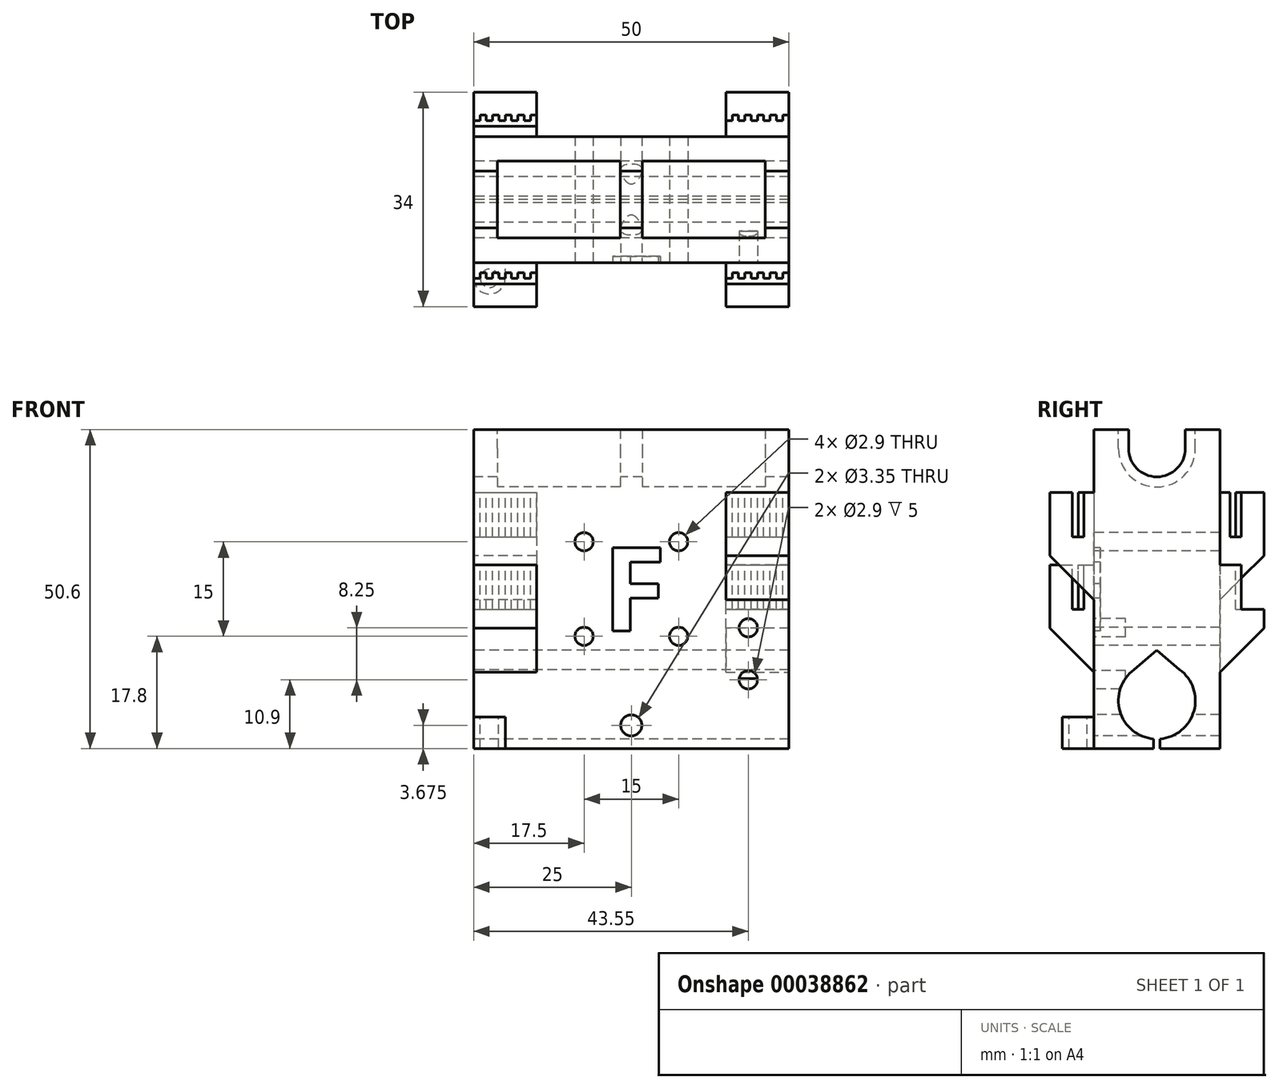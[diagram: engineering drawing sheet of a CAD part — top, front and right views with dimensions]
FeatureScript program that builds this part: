
annotation { "Feature Type Name" : "Feature", "Feature Type Description" : "" }
export const myFeature = defineFeature(function(context is Context, id is Id, definition is map)
    precondition{}
    {
        {
            assignVariable(context, id + "F0", {"name" : "LM8LUU", "anyValue" : 0});
        }
        {
            var Q0;
            Q0=qCreatedBy(makeId("Top.planeOp"),FACE);
            var sketch = newSketch(context, id + "F1", { "sketchPlane" : qUnion([Q0])});
            skLineSegment(sketch, "E0.bottom", {"start": v(0, 0) * mm, "end": v(50, 0) * mm});
            skLineSegment(sketch, "E0.top", {"start": v(0, 20) * mm, "end": v(50, 20) * mm});
            skLineSegment(sketch, "E0.left", {"start": v(0, 0) * mm, "end": v(0, 20) * mm});
            skLineSegment(sketch, "E0.right", {"start": v(50, 0) * mm, "end": v(50, 20) * mm});
            skSolve(sketch);
        }
        {
            var Q0;
            Q0=qSketchRegion(id+"F1",true);
            extrude(context, id + "F2", {"entities" : qUnion([Q0]), "depth" : 50.6 * mm});
        }
        {
            var Q0;
            Q0=makeQuery(id+"F2.opExtrude","SWEPT_FACE",FACE,{"disambiguationData":[OSD([sQuery(id+"F1.wireOp",EDGE,"E0.left")])]});
            var sketch = newSketch(context, id + "F3", { "sketchPlane" : qUnion([Q0])});
            skCircle(sketch, "E1", {"center": v(-10, 7.6) * mm, "radius": 6.1 * mm});
            skCircle(sketch, "E2", {"center": v(-10, 47.6) * mm, "radius": 4.5 * mm});
            skLineSegment(sketch, "E3", {"start": v(-20, 47.6) * mm, "end": v(0, 47.6) * mm, "construction": true});
            skLineSegment(sketch, "E4", {"start": v(-14.5, 50.6) * mm, "end": v(-14.5, 47.6) * mm});
            skLineSegment(sketch, "E5", {"start": v(-5.5, 50.6) * mm, "end": v(-5.5, 47.6) * mm});
            skLineSegment(sketch, "E6", {"start": v(-20, 7.6) * mm, "end": v(0, 7.6) * mm, "construction": true});
            skLineSegment(sketch, "E7", {"start": v(-10, 7.6) * mm, "end": v(-10, 0) * mm, "construction": true});
            skLineSegment(sketch, "E8", {"start": v(-10, 0) * mm, "end": v(-10.5, 0) * mm});
            skLineSegment(sketch, "E9", {"start": v(-10.5, 0) * mm, "end": v(-10.5, 1.52) * mm});
            skLineSegment(sketch, "E10", {"start": v(-10.5, 1.52) * mm, "end": v(-9.5, 1.52) * mm});
            skLineSegment(sketch, "E11", {"start": v(-9.5, 1.52) * mm, "end": v(-9.5, 0) * mm});
            skLineSegment(sketch, "E12", {"start": v(-9.5, 0) * mm, "end": v(-10, 0) * mm});
            skLineSegment(sketch, "E13", {"start": v(-10, 13.7) * mm, "end": v(-10, 15.6) * mm});
            skLineSegment(sketch, "E14", {"start": v(-10, 15.6) * mm, "end": v(-6.39, 12.51) * mm});
            skLineSegment(sketch, "E15", {"start": v(-10, 15.6) * mm, "end": v(-13.61, 12.51) * mm});
            skCircle(sketch, "E16", {"center": v(-10, 47.6) * mm, "radius": 6.1 * mm});
            skLineSegment(sketch, "E17", {"start": v(-3.9, 47.6) * mm, "end": v(-3.9, 50.6) * mm});
            skLineSegment(sketch, "E18", {"start": v(-16.1, 47.6) * mm, "end": v(-16.1, 50.6) * mm});
            skSolve(sketch);
        }
        {
            var Q0;
            {var subQ0=sQuery(id+"F3.wireOp",EDGE,"E14");var subQ1=sQuery(id+"F3.wireOp",EDGE,"E1");var subQ3=makeQuery(id+"F3.imprint","INTERSECT",VERTEX,{"disambiguationData":[OD(0.0)],"derivedFrom":[subQ1,subQ0]});Q0=makeQuery(id+"F3.imprint","IMPRINT",FACE,{"disambiguationData":[TD([[makeQuery(id+"F3.imprint","IMPRINT",EDGE,{"disambiguationData":[TD([[subQ3,-1.0]])],"derivedFrom":subQ1}),1.0]])]});}
            var Q1;
            {var subQ0=sQuery(id+"F3.wireOp",EDGE,"E15");var subQ1=sQuery(id+"F3.wireOp",EDGE,"E1");var subQ3=makeQuery(id+"F3.imprint","INTERSECT",VERTEX,{"disambiguationData":[OD(0.0)],"derivedFrom":[subQ1,subQ0]});Q1=makeQuery(id+"F3.imprint","IMPRINT",FACE,{"disambiguationData":[TD([[makeQuery(id+"F3.imprint","IMPRINT",EDGE,{"disambiguationData":[TD([[subQ3,1.0]])],"derivedFrom":subQ1}),1.0]])]});}
            var Q2;
            Q2=makeQuery(id+"F3.imprint","IMPRINT",FACE,{"disambiguationData":[TD([[makeQuery(id+"F3.imprint","IMPRINT",EDGE,{"derivedFrom":sQuery(id+"F3.wireOp",EDGE,"E8")}),-1.0]])]});
            var Q3;
            {var subQ0=sQuery(id+"F3.wireOp",EDGE,"E10");Q3=makeQuery(id+"F3.imprint","IMPRINT",FACE,{"disambiguationData":[TD([[makeQuery(id+"F3.imprint","IMPRINT",EDGE,{"derivedFrom":subQ0}),-1.0]])]});}
            var Q4;
            {var subQ3=sQuery(id+"F3.wireOp",EDGE,"E13");Q4=makeQuery(id+"F3.imprint","IMPRINT",FACE,{"disambiguationData":[TD([[makeQuery(id+"F3.imprint","IMPRINT",EDGE,{"derivedFrom":subQ3}),-1.0]])]});}
            var Q5;
            {var subQ3=sQuery(id+"F3.wireOp",EDGE,"E13");Q5=makeQuery(id+"F3.imprint","IMPRINT",FACE,{"disambiguationData":[TD([[makeQuery(id+"F3.imprint","IMPRINT",EDGE,{"derivedFrom":subQ3}),1.0]])]});}
            var Q6;
            {var subQ7=sQuery(id+"F3.wireOp",EDGE,"E10");Q6=makeQuery(id+"F3.imprint","IMPRINT",FACE,{"disambiguationData":[TD([[makeQuery(id+"F3.imprint","IMPRINT",EDGE,{"derivedFrom":subQ7}),1.0]])]});}
            var Q7;
            {var subQ3=sQuery(id+"F3.wireOp",EDGE,"E5");Q7=makeQuery(id+"F3.imprint","IMPRINT",FACE,{"disambiguationData":[TD([[makeQuery(id+"F3.imprint","IMPRINT",EDGE,{"derivedFrom":subQ3}),-1.0]])]});}
            var Q8;
            {var subQ0=sQuery(id+"F3.wireOp",EDGE,"E4");Q8=makeQuery(id+"F3.imprint","IMPRINT",FACE,{"disambiguationData":[TD([[makeQuery(id+"F3.imprint","IMPRINT",EDGE,{"derivedFrom":subQ0}),1.0]])]});}
            var Q9;
            {var subQ0=sQuery(id+"F3.wireOp",EDGE,"E4");Q9=makeQuery(id+"F3.imprint","IMPRINT",FACE,{"disambiguationData":[TD([[makeQuery(id+"F3.imprint","IMPRINT",EDGE,{"derivedFrom":subQ0}),1.0]])]});}
            var Q10;
            {var subQ3=sQuery(id+"F3.wireOp",EDGE,"E5");Q10=makeQuery(id+"F3.imprint","IMPRINT",FACE,{"disambiguationData":[TD([[makeQuery(id+"F3.imprint","IMPRINT",EDGE,{"derivedFrom":subQ3}),-1.0]])]});}
            var Q11;
            {var subQ1=sQuery(id+"F3.wireOp",EDGE,"E2");var subQ4=makeQuery(id+"F3.imprint","INTERSECT",VERTEX,{"derivedFrom":[subQ1,sQuery(id+"F3.wireOp",EDGE,"E5")]});Q11=makeQuery(id+"F3.imprint","IMPRINT",FACE,{"disambiguationData":[TD([[makeQuery(id+"F3.imprint","IMPRINT",EDGE,{"disambiguationData":[TD([[subQ4,-1.0]])],"derivedFrom":subQ1}),1.0]])]});}
            extrude(context, id + "F4", {"entities" : qUnion([Q0, Q1, Q2, Q3, Q4, Q5, Q6, Q7, Q8, Q9, Q10, Q11]), "operationType" : NewBodyOperationType.REMOVE, "endBound" : BoundingType.THROUGH_ALL, "oppositeDirection" : true, "depth" : 25 * mm});
        }
        {
            var Q0;
            {var subQ3=sQuery(id+"F3.wireOp",EDGE,"E4");Q0=makeQuery(id+"F3.imprint","IMPRINT",FACE,{"disambiguationData":[TD([[makeQuery(id+"F3.imprint","IMPRINT",EDGE,{"derivedFrom":subQ3}),-1.0]])]});}
            var Q1;
            {var subQ3=sQuery(id+"F3.wireOp",EDGE,"E18");Q1=makeQuery(id+"F3.imprint","IMPRINT",FACE,{"disambiguationData":[TD([[makeQuery(id+"F3.imprint","IMPRINT",EDGE,{"derivedFrom":subQ3}),-1.0]])]});}
            var Q2;
            {var subQ3=sQuery(id+"F3.wireOp",EDGE,"E17");Q2=makeQuery(id+"F3.imprint","IMPRINT",FACE,{"disambiguationData":[TD([[makeQuery(id+"F3.imprint","IMPRINT",EDGE,{"derivedFrom":subQ3}),1.0]])]});}
            extrude(context, id + "F5", {"entities" : qUnion([Q0, Q1, Q2]), "operationType" : NewBodyOperationType.REMOVE, "oppositeDirection" : true, "depth" : (46.25 + getVariable(context, 'LM8LUU') * 2) * mm});
        }
        {
            var Q0;
            {var subQ3=sQuery(id+"F3.wireOp",EDGE,"E4");Q0=makeQuery(id+"F3.imprint","IMPRINT",FACE,{"disambiguationData":[TD([[makeQuery(id+"F3.imprint","IMPRINT",EDGE,{"derivedFrom":subQ3}),-1.0]])]});}
            var Q1;
            {var subQ3=sQuery(id+"F3.wireOp",EDGE,"E18");Q1=makeQuery(id+"F3.imprint","IMPRINT",FACE,{"disambiguationData":[TD([[makeQuery(id+"F3.imprint","IMPRINT",EDGE,{"derivedFrom":subQ3}),-1.0]])]});}
            var Q2;
            {var subQ3=sQuery(id+"F3.wireOp",EDGE,"E17");Q2=makeQuery(id+"F3.imprint","IMPRINT",FACE,{"disambiguationData":[TD([[makeQuery(id+"F3.imprint","IMPRINT",EDGE,{"derivedFrom":subQ3}),1.0]])]});}
            extrude(context, id + "F6", {"entities" : qUnion([Q0, Q1, Q2]), "operationType" : NewBodyOperationType.ADD, "oppositeDirection" : true, "depth" : (26.75 - getVariable(context, 'LM8LUU')) * mm});
        }
        {
            var Q0;
            {var subQ3=sQuery(id+"F3.wireOp",EDGE,"E4");Q0=makeQuery(id+"F3.imprint","IMPRINT",FACE,{"disambiguationData":[TD([[makeQuery(id+"F3.imprint","IMPRINT",EDGE,{"derivedFrom":subQ3}),-1.0]])]});}
            var Q1;
            {var subQ3=sQuery(id+"F3.wireOp",EDGE,"E18");Q1=makeQuery(id+"F3.imprint","IMPRINT",FACE,{"disambiguationData":[TD([[makeQuery(id+"F3.imprint","IMPRINT",EDGE,{"derivedFrom":subQ3}),-1.0]])]});}
            var Q2;
            {var subQ3=sQuery(id+"F3.wireOp",EDGE,"E17");Q2=makeQuery(id+"F3.imprint","IMPRINT",FACE,{"disambiguationData":[TD([[makeQuery(id+"F3.imprint","IMPRINT",EDGE,{"derivedFrom":subQ3}),1.0]])]});}
            extrude(context, id + "F7", {"entities" : qUnion([Q0, Q1, Q2]), "operationType" : NewBodyOperationType.REMOVE, "oppositeDirection" : true, "depth" : (23.25 + getVariable(context, 'LM8LUU')) * mm});
        }
        {
            var Q0;
            {var subQ3=sQuery(id+"F3.wireOp",EDGE,"E4");Q0=makeQuery(id+"F3.imprint","IMPRINT",FACE,{"disambiguationData":[TD([[makeQuery(id+"F3.imprint","IMPRINT",EDGE,{"derivedFrom":subQ3}),-1.0]])]});}
            var Q1;
            {var subQ3=sQuery(id+"F3.wireOp",EDGE,"E18");Q1=makeQuery(id+"F3.imprint","IMPRINT",FACE,{"disambiguationData":[TD([[makeQuery(id+"F3.imprint","IMPRINT",EDGE,{"derivedFrom":subQ3}),-1.0]])]});}
            var Q2;
            {var subQ3=sQuery(id+"F3.wireOp",EDGE,"E17");Q2=makeQuery(id+"F3.imprint","IMPRINT",FACE,{"disambiguationData":[TD([[makeQuery(id+"F3.imprint","IMPRINT",EDGE,{"derivedFrom":subQ3}),1.0]])]});}
            extrude(context, id + "F8", {"entities" : qUnion([Q0, Q1, Q2]), "operationType" : NewBodyOperationType.ADD, "oppositeDirection" : true, "depth" : 3.75 * mm});
        }
        {
            var Q0;
            Q0=makeQuery(id+"F2.opExtrude","SWEPT_FACE",FACE,{"disambiguationData":[OSD([sQuery(id+"F1.wireOp",EDGE,"E0.bottom")])]});
            var sketch = newSketch(context, id + "F9", { "sketchPlane" : qUnion([Q0])});
            skLineSegment(sketch, "E19.bottom", {"start": v(0, 29.1) * mm, "end": v(10, 29.1) * mm});
            skLineSegment(sketch, "E19.top", {"start": v(0, 9.1) * mm, "end": v(10, 9.1) * mm});
            skLineSegment(sketch, "E19.left", {"start": v(0, 29.1) * mm, "end": v(0, 9.1) * mm});
            skLineSegment(sketch, "E19.right", {"start": v(10, 29.1) * mm, "end": v(10, 9.1) * mm});
            skLineSegment(sketch, "E20.bottom", {"start": v(50, 40.6) * mm, "end": v(40, 40.6) * mm});
            skLineSegment(sketch, "E20.top", {"start": v(50, 20.6) * mm, "end": v(40, 20.6) * mm});
            skLineSegment(sketch, "E20.left", {"start": v(50, 40.6) * mm, "end": v(50, 20.6) * mm});
            skLineSegment(sketch, "E20.right", {"start": v(40, 40.6) * mm, "end": v(40, 20.6) * mm});
            skPoint(sketch, "E21", {"position": v(0, 47.6) * mm});
            skPoint(sketch, "E22", {"position": v(0, 8.6) * mm});
            skSolve(sketch);
        }
        {
            var Q0;
            Q0=qSketchRegion(id+"F9",true);
            extrude(context, id + "F10", {"entities" : qUnion([Q0]), "operationType" : NewBodyOperationType.ADD, "depth" : 7 * mm});
        }
        {
            var Q0;
            Q0=makeQuery(id+"F10.opExtrude","CAP_EDGE",EDGE,{"disambiguationData":[OSD([sQuery(id+"F9.wireOp",EDGE,"E19.top")])],"isStart":false});
            var Q1;
            Q1=makeQuery(id+"F10.opExtrude","CAP_EDGE",EDGE,{"disambiguationData":[OSD([sQuery(id+"F9.wireOp",EDGE,"E20.top")])],"isStart":false});
            chamfer(context, id + "F11", {"entities" : qUnion([Q0, Q1]), "width" : 10 * mm, "tangentPropagation" : true});
        }
        {
            var Q0;
            Q0=makeQuery(id+"F10.opExtrude","SWEPT_FACE",FACE,{"disambiguationData":[OSD([sQuery(id+"F9.wireOp",EDGE,"E19.bottom")])]});
            var sketch = newSketch(context, id + "F12", { "sketchPlane" : qUnion([Q0])});
            skLineSegment(sketch, "E23", {"start": v(-935.9, 0) * mm, "end": v(-935.88, -4.54) * mm});
            skLineSegment(sketch, "E24.left", {"start": v(0, -3.4) * mm, "end": v(0, -1.6) * mm});
            skLineSegment(sketch, "E25", {"start": v(6, -2.5) * mm, "end": v(7, -2.5) * mm});
            skLineSegment(sketch, "E26", {"start": v(4, -2.5) * mm, "end": v(5, -2.5) * mm});
            skLineSegment(sketch, "E27", {"start": v(0, -2.5) * mm, "end": v(1, -2.5) * mm});
            skLineSegment(sketch, "E28", {"start": v(7, -1.6) * mm, "end": v(8, -1.6) * mm});
            skLineSegment(sketch, "E29", {"start": v(2, -2.5) * mm, "end": v(3, -2.5) * mm});
            skLineSegment(sketch, "E30", {"start": v(3, -1.6) * mm, "end": v(4, -1.6) * mm});
            skLineSegment(sketch, "E31", {"start": v(8, -2.5) * mm, "end": v(9, -2.5) * mm});
            skLineSegment(sketch, "E32", {"start": v(8, -1.6) * mm, "end": v(8, -2.5) * mm});
            skLineSegment(sketch, "E33", {"start": v(9, -2.5) * mm, "end": v(9, -1.6) * mm});
            skLineSegment(sketch, "E34", {"start": v(10, -1.6) * mm, "end": v(10, -2.5) * mm});
            skLineSegment(sketch, "E35", {"start": v(6, -1.6) * mm, "end": v(6, -2.5) * mm});
            skLineSegment(sketch, "E36", {"start": v(2, -1.6) * mm, "end": v(2, -2.5) * mm});
            skLineSegment(sketch, "E37", {"start": v(1, -1.6) * mm, "end": v(2, -1.6) * mm});
            skLineSegment(sketch, "E38", {"start": v(1, -2.5) * mm, "end": v(1, -1.6) * mm});
            skLineSegment(sketch, "E39", {"start": v(9, -1.6) * mm, "end": v(10, -1.6) * mm});
            skLineSegment(sketch, "E40", {"start": v(5, -1.6) * mm, "end": v(6, -1.6) * mm});
            skLineSegment(sketch, "E41", {"start": v(5, -2.5) * mm, "end": v(5, -1.6) * mm});
            skLineSegment(sketch, "E42", {"start": v(3, -2.5) * mm, "end": v(3, -1.6) * mm});
            skLineSegment(sketch, "E43", {"start": v(4, -1.6) * mm, "end": v(4, -2.5) * mm});
            skLineSegment(sketch, "E44", {"start": v(7, -2.5) * mm, "end": v(7, -1.6) * mm});
            skLineSegment(sketch, "E45", {"start": v(0, -1.6) * mm, "end": v(0, -2.5) * mm});
            skLineSegment(sketch, "E46", {"start": v(10, -2.5) * mm, "end": v(10, -3.4) * mm});
            skLineSegment(sketch, "E47", {"start": v(0, -3.4) * mm, "end": v(10, -3.4) * mm});
            skLineSegment(sketch, "E48", {"start": v(5.3, -1.6) * mm, "end": v(5.3, 0) * mm});
            skSolve(sketch);
        }
        {
            var Q0;
            Q0=qSketchRegion(id+"F12",true);
            extrude(context, id + "F13", {"entities" : qUnion([Q0]), "operationType" : NewBodyOperationType.REMOVE, "oppositeDirection" : true, "depth" : 7 * mm});
        }
        {
            var Q0;
            Q0=makeQuery(id+"F10.opExtrude","SWEPT_FACE",FACE,{"disambiguationData":[OSD([sQuery(id+"F9.wireOp",EDGE,"E20.bottom")])]});
            var sketch = newSketch(context, id + "F14", { "sketchPlane" : qUnion([Q0])});
            skLineSegment(sketch, "E49.left", {"start": v(40, -3.4) * mm, "end": v(40, -1.6) * mm});
            skLineSegment(sketch, "E50", {"start": v(46, -2.5) * mm, "end": v(47, -2.5) * mm});
            skLineSegment(sketch, "E51", {"start": v(44, -2.5) * mm, "end": v(45, -2.5) * mm});
            skLineSegment(sketch, "E52", {"start": v(40, -2.5) * mm, "end": v(41, -2.5) * mm});
            skLineSegment(sketch, "E53", {"start": v(47, -1.6) * mm, "end": v(48, -1.6) * mm});
            skLineSegment(sketch, "E54", {"start": v(42, -2.5) * mm, "end": v(43, -2.5) * mm});
            skLineSegment(sketch, "E55", {"start": v(43, -1.6) * mm, "end": v(44, -1.6) * mm});
            skLineSegment(sketch, "E56", {"start": v(48, -2.5) * mm, "end": v(49, -2.5) * mm});
            skLineSegment(sketch, "E57", {"start": v(48, -1.6) * mm, "end": v(48, -2.5) * mm});
            skLineSegment(sketch, "E58", {"start": v(49, -2.5) * mm, "end": v(49, -1.6) * mm});
            skLineSegment(sketch, "E59", {"start": v(50, -1.6) * mm, "end": v(50, -2.5) * mm});
            skLineSegment(sketch, "E60", {"start": v(46, -1.6) * mm, "end": v(46, -2.5) * mm});
            skLineSegment(sketch, "E61", {"start": v(42, -1.6) * mm, "end": v(42, -2.5) * mm});
            skLineSegment(sketch, "E62", {"start": v(41, -1.6) * mm, "end": v(42, -1.6) * mm});
            skLineSegment(sketch, "E63", {"start": v(41, -2.5) * mm, "end": v(41, -1.6) * mm});
            skLineSegment(sketch, "E64", {"start": v(49, -1.6) * mm, "end": v(50, -1.6) * mm});
            skLineSegment(sketch, "E65", {"start": v(45, -1.6) * mm, "end": v(46, -1.6) * mm});
            skLineSegment(sketch, "E66", {"start": v(45, -2.5) * mm, "end": v(45, -1.6) * mm});
            skLineSegment(sketch, "E67", {"start": v(43, -2.5) * mm, "end": v(43, -1.6) * mm});
            skLineSegment(sketch, "E68", {"start": v(44, -1.6) * mm, "end": v(44, -2.5) * mm});
            skLineSegment(sketch, "E69", {"start": v(47, -2.5) * mm, "end": v(47, -1.6) * mm});
            skLineSegment(sketch, "E70", {"start": v(40, -1.6) * mm, "end": v(40, -2.5) * mm});
            skLineSegment(sketch, "E71", {"start": v(50, -2.5) * mm, "end": v(50, -3.4) * mm});
            skLineSegment(sketch, "E72", {"start": v(40, -3.4) * mm, "end": v(50, -3.4) * mm});
            skLineSegment(sketch, "E73", {"start": v(45.23, -1.6) * mm, "end": v(45.23, 0) * mm});
            skSolve(sketch);
        }
        {
            var Q0;
            Q0=qSketchRegion(id+"F14",true);
            extrude(context, id + "F15", {"entities" : qUnion([Q0]), "operationType" : NewBodyOperationType.REMOVE, "oppositeDirection" : true, "depth" : 7 * mm});
        }
        {
            var Q0;
            Q0=makeQuery(id+"F2.opExtrude","SWEPT_FACE",FACE,{"disambiguationData":[OSD([sQuery(id+"F1.wireOp",EDGE,"E0.top")])]});
            var sketch = newSketch(context, id + "F16", { "sketchPlane" : qUnion([Q0])});
            skLineSegment(sketch, "E74.bottom", {"start": v(-50, 9.1) * mm, "end": v(-40, 9.1) * mm});
            skLineSegment(sketch, "E74.top", {"start": v(-50, 29.1) * mm, "end": v(-40, 29.1) * mm});
            skLineSegment(sketch, "E74.left", {"start": v(-50, 9.1) * mm, "end": v(-50, 29.1) * mm});
            skLineSegment(sketch, "E74.right", {"start": v(-40, 9.1) * mm, "end": v(-40, 29.1) * mm});
            skLineSegment(sketch, "E75.bottom", {"start": v(0, 40.6) * mm, "end": v(-10, 40.6) * mm});
            skLineSegment(sketch, "E75.top", {"start": v(0, 20.6) * mm, "end": v(-10, 20.6) * mm});
            skLineSegment(sketch, "E75.left", {"start": v(0, 40.6) * mm, "end": v(0, 20.6) * mm});
            skLineSegment(sketch, "E75.right", {"start": v(-10, 40.6) * mm, "end": v(-10, 20.6) * mm});
            skSolve(sketch);
        }
        {
            var Q0;
            Q0=qSketchRegion(id+"F16",true);
            extrude(context, id + "F17", {"entities" : qUnion([Q0]), "operationType" : NewBodyOperationType.ADD, "depth" : 7 * mm});
        }
        {
            var Q0;
            Q0=makeQuery(id+"F17.opExtrude","SWEPT_FACE",FACE,{"disambiguationData":[OSD([sQuery(id+"F16.wireOp",EDGE,"E74.top")])]});
            var sketch = newSketch(context, id + "F18", { "sketchPlane" : qUnion([Q0])});
            skLineSegment(sketch, "E76.left", {"start": v(40, 21.6) * mm, "end": v(40, 23.4) * mm});
            skLineSegment(sketch, "E77", {"start": v(46, 22.5) * mm, "end": v(47, 22.5) * mm});
            skLineSegment(sketch, "E78", {"start": v(44, 22.5) * mm, "end": v(45, 22.5) * mm});
            skLineSegment(sketch, "E79", {"start": v(40, 22.5) * mm, "end": v(41, 22.5) * mm});
            skLineSegment(sketch, "E80", {"start": v(47, 23.4) * mm, "end": v(48, 23.4) * mm});
            skLineSegment(sketch, "E81", {"start": v(42, 22.5) * mm, "end": v(43, 22.5) * mm});
            skLineSegment(sketch, "E82", {"start": v(43, 23.4) * mm, "end": v(44, 23.4) * mm});
            skLineSegment(sketch, "E83", {"start": v(48, 22.5) * mm, "end": v(49, 22.5) * mm});
            skLineSegment(sketch, "E84", {"start": v(48, 23.4) * mm, "end": v(48, 22.5) * mm});
            skLineSegment(sketch, "E85", {"start": v(49, 22.5) * mm, "end": v(49, 23.4) * mm});
            skLineSegment(sketch, "E86", {"start": v(50, 23.4) * mm, "end": v(50, 22.5) * mm});
            skLineSegment(sketch, "E87", {"start": v(46, 23.4) * mm, "end": v(46, 22.5) * mm});
            skLineSegment(sketch, "E88", {"start": v(42, 23.4) * mm, "end": v(42, 22.5) * mm});
            skLineSegment(sketch, "E89", {"start": v(41, 23.4) * mm, "end": v(42, 23.4) * mm});
            skLineSegment(sketch, "E90", {"start": v(41, 22.5) * mm, "end": v(41, 23.4) * mm});
            skLineSegment(sketch, "E91", {"start": v(49, 23.4) * mm, "end": v(50, 23.4) * mm});
            skLineSegment(sketch, "E92", {"start": v(45, 23.4) * mm, "end": v(46, 23.4) * mm});
            skLineSegment(sketch, "E93", {"start": v(45, 22.5) * mm, "end": v(45, 23.4) * mm});
            skLineSegment(sketch, "E94", {"start": v(43, 22.5) * mm, "end": v(43, 23.4) * mm});
            skLineSegment(sketch, "E95", {"start": v(44, 23.4) * mm, "end": v(44, 22.5) * mm});
            skLineSegment(sketch, "E96", {"start": v(47, 22.5) * mm, "end": v(47, 23.4) * mm});
            skLineSegment(sketch, "E97", {"start": v(40, 23.4) * mm, "end": v(40, 22.5) * mm});
            skLineSegment(sketch, "E98", {"start": v(50, 22.5) * mm, "end": v(50, 21.6) * mm});
            skLineSegment(sketch, "E99", {"start": v(40, 21.6) * mm, "end": v(50, 21.6) * mm});
            skLineSegment(sketch, "E100", {"start": v(45, 21.6) * mm, "end": v(45, 20) * mm});
            skSolve(sketch);
        }
        {
            var Q0;
            {var subQ4=sQuery(id+"F18.wireOp",EDGE,"E76.left");Q0=makeQuery(id+"F18.imprint","IMPRINT",FACE,{"disambiguationData":[TD([[makeQuery(id+"F18.imprint","IMPRINT",EDGE,{"derivedFrom":subQ4}),1.0]])]});}
            extrude(context, id + "F19", {"entities" : qUnion([Q0]), "operationType" : NewBodyOperationType.REMOVE, "oppositeDirection" : true, "depth" : 7 * mm});
        }
        {
            var Q0;
            Q0=makeQuery(id+"F17.opExtrude","SWEPT_FACE",FACE,{"disambiguationData":[OSD([sQuery(id+"F16.wireOp",EDGE,"E75.bottom")])]});
            var sketch = newSketch(context, id + "F20", { "sketchPlane" : qUnion([Q0])});
            skLineSegment(sketch, "E101", {"start": v(6, 22.5) * mm, "end": v(7, 22.5) * mm});
            skLineSegment(sketch, "E102", {"start": v(4, 22.5) * mm, "end": v(5, 22.5) * mm});
            skLineSegment(sketch, "E103", {"start": v(0, 22.5) * mm, "end": v(1, 22.5) * mm});
            skLineSegment(sketch, "E104", {"start": v(7, 23.4) * mm, "end": v(8, 23.4) * mm});
            skLineSegment(sketch, "E105", {"start": v(2, 22.5) * mm, "end": v(3, 22.5) * mm});
            skLineSegment(sketch, "E106", {"start": v(3, 23.4) * mm, "end": v(4, 23.4) * mm});
            skLineSegment(sketch, "E107", {"start": v(8, 22.5) * mm, "end": v(9, 22.5) * mm});
            skLineSegment(sketch, "E108", {"start": v(8, 23.4) * mm, "end": v(8, 22.5) * mm});
            skLineSegment(sketch, "E109", {"start": v(9, 22.5) * mm, "end": v(9, 23.4) * mm});
            skLineSegment(sketch, "E110", {"start": v(10, 23.4) * mm, "end": v(10, 22.5) * mm});
            skLineSegment(sketch, "E111", {"start": v(6, 23.4) * mm, "end": v(6, 22.5) * mm});
            skLineSegment(sketch, "E112", {"start": v(2, 23.4) * mm, "end": v(2, 22.5) * mm});
            skLineSegment(sketch, "E113", {"start": v(1, 23.4) * mm, "end": v(2, 23.4) * mm});
            skLineSegment(sketch, "E114", {"start": v(1, 22.5) * mm, "end": v(1, 23.4) * mm});
            skLineSegment(sketch, "E115", {"start": v(9, 23.4) * mm, "end": v(10, 23.4) * mm});
            skLineSegment(sketch, "E116", {"start": v(5, 23.4) * mm, "end": v(6, 23.4) * mm});
            skLineSegment(sketch, "E117", {"start": v(5, 22.5) * mm, "end": v(5, 23.4) * mm});
            skLineSegment(sketch, "E118", {"start": v(3, 22.5) * mm, "end": v(3, 23.4) * mm});
            skLineSegment(sketch, "E119", {"start": v(4, 23.4) * mm, "end": v(4, 22.5) * mm});
            skLineSegment(sketch, "E120", {"start": v(7, 22.5) * mm, "end": v(7, 23.4) * mm});
            skLineSegment(sketch, "E121", {"start": v(10, 22.5) * mm, "end": v(10, 21.6) * mm});
            skLineSegment(sketch, "E122", {"start": v(0, 21.6) * mm, "end": v(10, 21.6) * mm});
            skLineSegment(sketch, "E123", {"start": v(5, 21.6) * mm, "end": v(5, 20) * mm});
            skLineSegment(sketch, "E124", {"start": v(0, 21.6) * mm, "end": v(0, 22.5) * mm});
            skSolve(sketch);
        }
        {
            var Q0;
            Q0=makeQuery(id+"F20.imprint","IMPRINT",FACE,{"disambiguationData":[TD([[makeQuery(id+"F20.imprint","IMPRINT",EDGE,{"derivedFrom":sQuery(id+"F20.wireOp",EDGE,"E101")}),-1.0]])]});
            extrude(context, id + "F21", {"entities" : qUnion([Q0]), "operationType" : NewBodyOperationType.REMOVE, "oppositeDirection" : true, "depth" : 7 * mm});
        }
        {
            var Q0;
            Q0=makeQuery(id+"F17.opExtrude","CAP_EDGE",EDGE,{"disambiguationData":[OSD([sQuery(id+"F16.wireOp",EDGE,"E75.top")])],"isStart":false});
            var Q1;
            Q1=makeQuery(id+"F17.opExtrude","CAP_EDGE",EDGE,{"disambiguationData":[OSD([sQuery(id+"F16.wireOp",EDGE,"E74.bottom")])],"isStart":false});
            chamfer(context, id + "F22", {"entities" : qUnion([Q0, Q1]), "width" : 10 * mm, "tangentPropagation" : true});
        }
        {
            var Q0;
            Q0=makeQuery(id+"F2.opExtrude","SWEPT_FACE",FACE,{"disambiguationData":[OSD([sQuery(id+"F1.wireOp",EDGE,"E0.bottom")])]});
            var sketch = newSketch(context, id + "F23", { "sketchPlane" : qUnion([Q0])});
            skCircle(sketch, "E125", {"center": v(17.5, 32.8) * mm, "radius": 1.45 * mm});
            skCircle(sketch, "E126", {"center": v(32.5, 32.8) * mm, "radius": 1.45 * mm});
            skCircle(sketch, "E127", {"center": v(17.5, 17.8) * mm, "radius": 1.45 * mm});
            skCircle(sketch, "E128", {"center": v(32.5, 17.8) * mm, "radius": 1.45 * mm});
            skLineSegment(sketch, "E129", {"start": v(17.5, 32.8) * mm, "end": v(0, 32.8) * mm});
            skLineSegment(sketch, "E130", {"start": v(32.5, 17.8) * mm, "end": v(50, 17.8) * mm});
            skLineSegment(sketch, "E131", {"start": v(32.5, 32.8) * mm, "end": v(32.5, 50.6) * mm});
            skLineSegment(sketch, "E132", {"start": v(17.5, 17.8) * mm, "end": v(17.5, 0) * mm});
            skCircle(sketch, "E133", {"center": v(25, 3.68) * mm, "radius": 1.68 * mm});
            skLineSegment(sketch, "E134", {"start": v(25, 0) * mm, "end": v(25, 13.82) * mm, "construction": true});
            skSolve(sketch);
        }
        {
            var Q0;
            Q0=qSketchRegion(id+"F23",true);
            var Q1;
            Q1=makeQuery(id+"F23.imprint","IMPRINT",FACE,{"disambiguationData":[TD([[makeQuery(id+"F23.imprint","IMPRINT",EDGE,{"derivedFrom":sQuery(id+"F23.wireOp",EDGE,"E125")}),1.0]])]});
            var Q2;
            Q2=makeQuery(id+"F23.imprint","IMPRINT",FACE,{"disambiguationData":[TD([[makeQuery(id+"F23.imprint","IMPRINT",EDGE,{"derivedFrom":sQuery(id+"F23.wireOp",EDGE,"E126")}),1.0]])]});
            var Q3;
            Q3=makeQuery(id+"F23.imprint","IMPRINT",FACE,{"disambiguationData":[TD([[makeQuery(id+"F23.imprint","IMPRINT",EDGE,{"derivedFrom":sQuery(id+"F23.wireOp",EDGE,"E128")}),1.0]])]});
            var Q4;
            Q4=makeQuery(id+"F23.imprint","IMPRINT",FACE,{"disambiguationData":[TD([[makeQuery(id+"F23.imprint","IMPRINT",EDGE,{"derivedFrom":sQuery(id+"F23.wireOp",EDGE,"E127")}),1.0]])]});
            extrude(context, id + "F24", {"entities" : qUnion([Q0, Q1, Q2, Q3, Q4]), "operationType" : NewBodyOperationType.REMOVE, "endBound" : BoundingType.THROUGH_ALL, "oppositeDirection" : true, "depth" : 25 * mm});
        }
        {
            var Q0;
            Q0=makeQuery(id+"F2.opExtrude","SWEPT_FACE",FACE,{"disambiguationData":[OSD([sQuery(id+"F1.wireOp",EDGE,"E0.bottom")])]});
            var sketch = newSketch(context, id + "F25", { "sketchPlane" : qUnion([Q0])});
            skCircle(sketch, "E135", {"center": v(43.55, 19.15) * mm, "radius": 1.45 * mm});
            skCircle(sketch, "E136", {"center": v(43.55, 10.9) * mm, "radius": 1.45 * mm});
            skSolve(sketch);
        }
        {
            var Q0;
            Q0=qSketchRegion(id+"F25",true);
            extrude(context, id + "F26", {"entities" : qUnion([Q0]), "operationType" : NewBodyOperationType.REMOVE, "oppositeDirection" : true, "depth" : 5 * mm});
        }
        {
            var Q0;
            Q0=makeQuery(id+"F2.opExtrude","SWEPT_FACE",FACE,{"disambiguationData":[OSD([sQuery(id+"F1.wireOp",EDGE,"E0.bottom")])]});
            var sketch = newSketch(context, id + "F27", { "sketchPlane" : qUnion([Q0])});
            skText(sketch, "E137", { "text": "F", "fontName": "OpenSans-Bold.ttf"});
            skLineSegment(sketch, "E138", {"start": v(17.5, 32.8) * mm, "end": v(17.5, 17.8) * mm, "construction": true});
            skLineSegment(sketch, "E139", {"start": v(17.5, 17.8) * mm, "end": v(32.5, 17.8) * mm, "construction": true});
            skLineSegment(sketch, "E140", {"start": v(32.5, 17.8) * mm, "end": v(32.5, 32.8) * mm, "construction": true});
            skLineSegment(sketch, "E141", {"start": v(32.5, 32.8) * mm, "end": v(17.5, 32.8) * mm, "construction": true});
            skLineSegment(sketch, "E142", {"start": v(17.5, 25.3) * mm, "end": v(20.4, 25.3) * mm, "construction": true});
            skLineSegment(sketch, "E143", {"start": v(29.6, 25.3) * mm, "end": v(32.5, 25.3) * mm, "construction": true});
            skLineSegment(sketch, "E144", {"start": v(25, 18.66) * mm, "end": v(25, 17.8) * mm, "construction": true});
            skLineSegment(sketch, "E145", {"start": v(25, 32.8) * mm, "end": v(25, 31.94) * mm, "construction": true});
            const initialGuessF27  = {"E137": [0.0204, 0.01866, 1, 0, 0.01328]};
            skSetInitialGuess(sketch, initialGuessF27);
            skSolve(sketch);
        }
        {
            var Q0;
            Q0=qSketchRegion(id+"F27",true);
            extrude(context, id + "F28", {"entities" : qUnion([Q0]), "operationType" : NewBodyOperationType.REMOVE, "oppositeDirection" : true, "depth" : 1 * mm});
        }
        {
            var Q0;
            Q0=makeQuery(id+"F2.opExtrude","SWEPT_FACE",FACE,{"disambiguationData":[OSD([sQuery(id+"F1.wireOp",EDGE,"E0.bottom")])]});
            var sketch = newSketch(context, id + "F29", { "sketchPlane" : qUnion([Q0])});
            skLineSegment(sketch, "E146.bottom", {"start": v(0, 0) * mm, "end": v(5, 0) * mm});
            skLineSegment(sketch, "E146.top", {"start": v(0, 5) * mm, "end": v(5, 5) * mm});
            skLineSegment(sketch, "E146.left", {"start": v(0, 0) * mm, "end": v(0, 5) * mm});
            skLineSegment(sketch, "E146.right", {"start": v(5, 0) * mm, "end": v(5, 5) * mm});
            skSolve(sketch);
        }
        {
            var Q0;
            Q0=qSketchRegion(id+"F29",true);
            extrude(context, id + "F30", {"entities" : qUnion([Q0]), "operationType" : NewBodyOperationType.ADD, "depth" : 5 * mm});
        }
        {
            var Q0;
            Q0=makeQuery(id+"F30.opExtrude","SWEPT_FACE",FACE,{"disambiguationData":[OSD([sQuery(id+"F29.wireOp",EDGE,"E146.top")])]});
            var sketch = newSketch(context, id + "F31", { "sketchPlane" : qUnion([Q0])});
            skCircle(sketch, "E147", {"center": v(2.5, -2.5) * mm, "radius": 1.45 * mm});
            skLineSegment(sketch, "E148", {"start": v(0, -2.5) * mm, "end": v(5, -2.5) * mm});
            skSolve(sketch);
        }
        {
            var Q0;
            Q0=qSketchRegion(id+"F31",true);
            extrude(context, id + "F32", {"entities" : qUnion([Q0]), "operationType" : NewBodyOperationType.REMOVE, "oppositeDirection" : true, "depth" : 25 * mm});
        }
        {
            var Q0;
            Q0=makeQuery(id+"F30.opExtrude","CAP_EDGE",EDGE,{"disambiguationData":[OSD([sQuery(id+"F29.wireOp",EDGE,"E146.left")])],"isStart":false});
            var Q1;
            Q1=makeQuery(id+"F30.opExtrude","CAP_EDGE",EDGE,{"disambiguationData":[OSD([sQuery(id+"F29.wireOp",EDGE,"E146.right")])],"isStart":false});
            fillet(context, id + "F33", {"entities" : qUnion([Q0, Q1]), "radius" : 2.5 * mm, "tangentPropagation" : true, "allowEdgeOverflow" : false});
        }
    });
